# Revit family: QF_BOURGEAT_Satellite4GT_froid_1-1_entree325_vitree_ouverture_droite
name_source: partatom
category: Equipement spécialisé
revit_build: Autodesk Revit 2015 (Build: 20140606_1530(x64)
units: mm (PartAtom-declared; Revit-internal decimal feet)

## types (1)
- GN14_porte_vitree_tirant_droit
    Certification = NF hygiene alimentaire
    Charge max = 140.00 kg
    Charge_gaz = 0.150 Kg
    Classe Climatique = 4
    Consommation énergétique = 3.2 Kwh/h NFD40-016
    Diametre_roue = 160 mm  [stored 0.524934 ft]
    Dimension_verticale_vitre = 704 mm  [stored 2.30971 ft]
    Fabricant = BOURGEAT
    Fréquence = 50 Hz
    Hauteur hors tout = 1575 mm  [stored 5.16732 ft]
    Hauteur_poignee_porte_sol = 600 mm
    Hauteur_poignees_laterales = 936 mm  [stored 3.07087 ft]
    Hauteur_porte = 1328 mm
    Hauteur_roue = 200 mm  [stored 0.656168 ft]
    Indice de protection = IP25
    Intensité nominale = 1 A
    Largeur_porte = 500 mm  [stored 1.64042 ft]
    Longueur hors tout = 585 mm  [stored 1.91929 ft]
    Longueur_poignees_laterales = 755 mm  [stored 2.47703 ft]
    Materiau_Poignee_porte = B_Elastomère_TPE_S
    Materiau_bac = B_Elastomère_TPE_S
    Materiau_bandage = B_Elastomère_TPE_S
    Materiau_glissiere = Acrylique, transparent
    Materiau_porte = Acier inoxydable, brossé
    Materiau_vitre = Verre, vitrage transparent, trempé
    Modèle = 842714 + 844000
    Nature isolant = Mousse sans PU
    Phase = 2
    Poids net à vide = 90.00 kg
    Pos_IHM_bord_gauche_porte_droite = 350 mm  [stored 1.14829 ft]
    Pos_V_IHM = 98 mm  [stored 0.321522 ft]
    Pos_vitre_bord_gauche_porte_droite = 102 mm
    Profondeur hors tout = 911 mm  [stored 2.98885 ft]
    Puissance frigorifique = 270 W à -5°C
    Puissance électrique  = 300 W
    Spécification du Fabricant = Satellite 4GT
    Tension = 230 V
    Type Fluide Frigorigène = R134a
    URL catalogue = http://www.bourgeat.fr

note: [stored X ft] marks values corroborated as IEEE doubles in the binary element streams (Revit-internal decimal feet)
